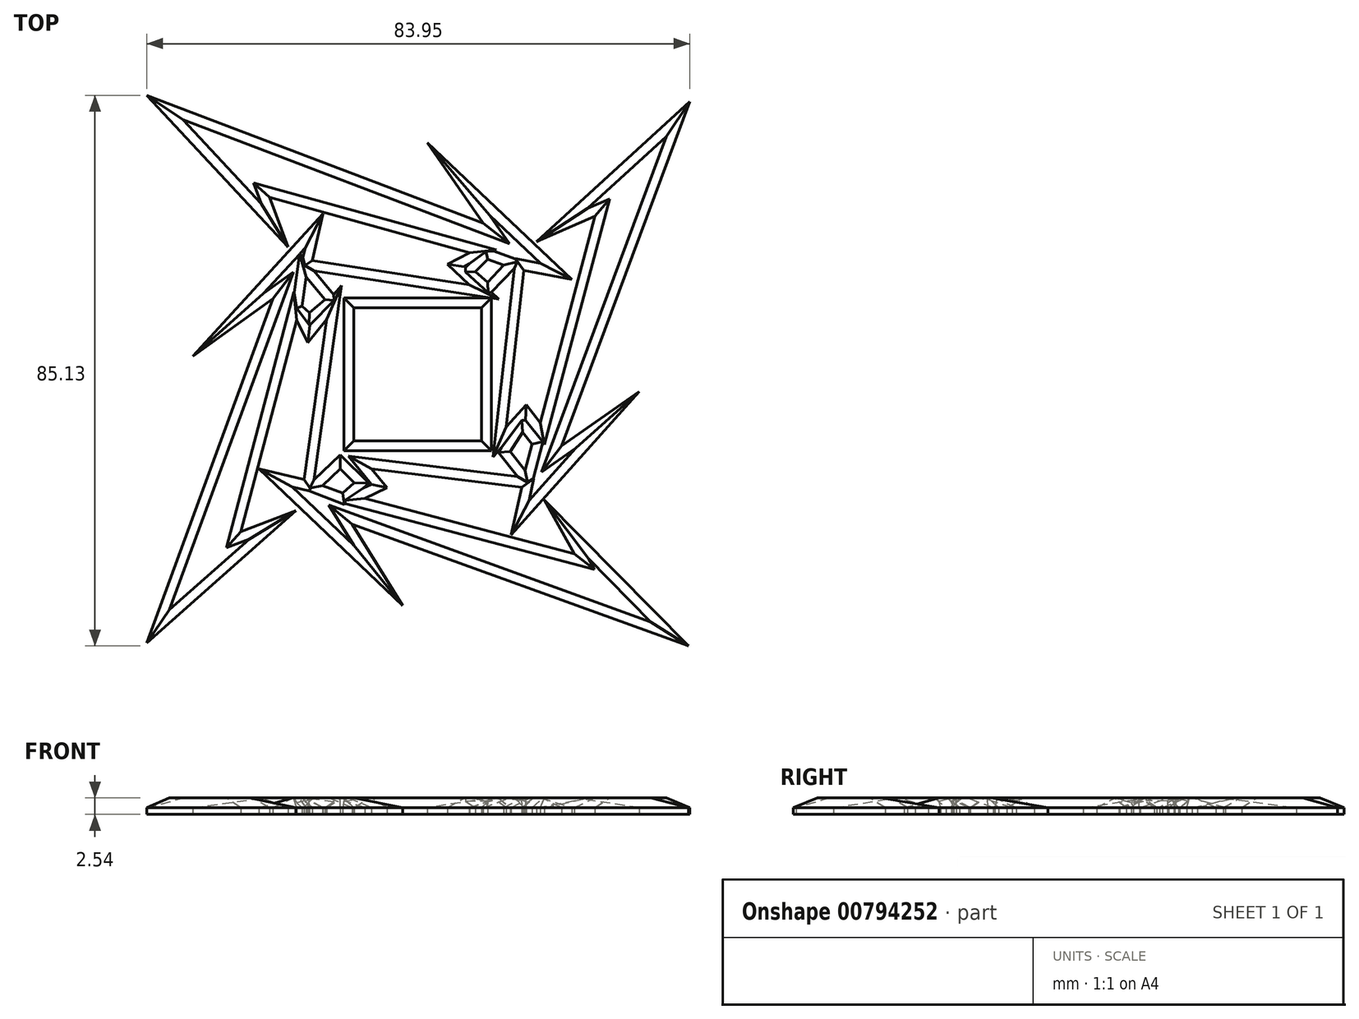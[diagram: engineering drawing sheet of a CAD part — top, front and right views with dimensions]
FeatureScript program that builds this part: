
annotation { "Feature Type Name" : "Feature", "Feature Type Description" : "" }
export const myFeature = defineFeature(function(context is Context, id is Id, definition is map)
    precondition{}
    {
        {
            var Q0;
            Q0=qCreatedBy(makeId("Top.planeOp"),FACE);
            var sketch = newSketch(context, id + "F0", { "sketchPlane" : qUnion([Q0])});
            skLineSegment(sketch, "E0", {"start": v(-34.9, 3.4) * mm, "end": v(-22.53, 12.24) * mm});
            skLineSegment(sketch, "E1", {"start": v(-22.53, 12.24) * mm, "end": v(-42.04, -40.95) * mm});
            skLineSegment(sketch, "E2", {"start": v(-42.04, -40.95) * mm, "end": v(-18.95, -20.5) * mm});
            skLineSegment(sketch, "E3", {"start": v(-18.95, -20.5) * mm, "end": v(-27.52, -23.74) * mm});
            skLineSegment(sketch, "E4", {"start": v(-18.87, 8.96) * mm, "end": v(-17.14, 5.48) * mm});
            skLineSegment(sketch, "E5", {"start": v(-17.14, 5.48) * mm, "end": v(-14.24, 9.08) * mm});
            skLineSegment(sketch, "E6", {"start": v(-14.24, 9.08) * mm, "end": v(-17.7, -15.71) * mm});
            skLineSegment(sketch, "E7", {"start": v(-17.7, -15.71) * mm, "end": v(-24.7, -14.04) * mm});
            skLineSegment(sketch, "E8", {"start": v(-24.7, -14.04) * mm, "end": v(-2.46, -35.16) * mm});
            skLineSegment(sketch, "E9", {"start": v(-2.46, -35.16) * mm, "end": v(-10.3, -22.58) * mm});
            skLineSegment(sketch, "E10", {"start": v(-10.3, -22.58) * mm, "end": v(41.73, -41.42) * mm});
            skLineSegment(sketch, "E11", {"start": v(41.73, -41.42) * mm, "end": v(19.46, -18.88) * mm});
            skLineSegment(sketch, "E12", {"start": v(19.46, -18.88) * mm, "end": v(24.08, -27.17) * mm});
            skLineSegment(sketch, "E13", {"start": v(24.08, -27.17) * mm, "end": v(-8.32, -18.6) * mm});
            skLineSegment(sketch, "E14", {"start": v(-8.32, -18.6) * mm, "end": v(-4.87, -16.98) * mm});
            skLineSegment(sketch, "E15", {"start": v(-4.87, -16.98) * mm, "end": v(-7.28, -14.04) * mm});
            skLineSegment(sketch, "E16", {"start": v(-7.28, -14.04) * mm, "end": v(15.96, -16.86) * mm});
            skLineSegment(sketch, "E17", {"start": v(15.96, -16.86) * mm, "end": v(14.3, -24.29) * mm});
            skLineSegment(sketch, "E18", {"start": v(34.13, -2.07) * mm, "end": v(22.1, -10.48) * mm});
            skLineSegment(sketch, "E19", {"start": v(22.1, -10.48) * mm, "end": v(41.9, 42.75) * mm});
            skLineSegment(sketch, "E20", {"start": v(41.9, 42.75) * mm, "end": v(18.25, 21.08) * mm});
            skLineSegment(sketch, "E21", {"start": v(18.25, 21.08) * mm, "end": v(27.23, 25.04) * mm});
            skLineSegment(sketch, "E22", {"start": v(27.23, 25.04) * mm, "end": v(18.78, -6.94) * mm});
            skLineSegment(sketch, "E23", {"start": v(18.78, -6.94) * mm, "end": v(16.6, -4.14) * mm});
            skLineSegment(sketch, "E24", {"start": v(16.6, -4.14) * mm, "end": v(13.54, -7.58) * mm});
            skLineSegment(sketch, "E25", {"start": v(13.54, -7.58) * mm, "end": v(16.28, 16.65) * mm});
            skLineSegment(sketch, "E26", {"start": v(16.28, 16.65) * mm, "end": v(23.7, 15.23) * mm});
            skLineSegment(sketch, "E27", {"start": v(1.34, 36.4) * mm, "end": v(10, 23.93) * mm});
            skLineSegment(sketch, "E28", {"start": v(10, 23.93) * mm, "end": v(-42.03, 43.71) * mm});
            skLineSegment(sketch, "E29", {"start": v(-42.03, 43.71) * mm, "end": v(-20.2, 20.25) * mm});
            skLineSegment(sketch, "E30", {"start": v(-20.2, 20.25) * mm, "end": v(-23.08, 27.92) * mm});
            skLineSegment(sketch, "E31", {"start": v(-23.08, 27.92) * mm, "end": v(7.87, 19.39) * mm});
            skLineSegment(sketch, "E32", {"start": v(7.87, 19.39) * mm, "end": v(4.46, 17.59) * mm});
            skLineSegment(sketch, "E33", {"start": v(4.46, 17.59) * mm, "end": v(7.8, 14.42) * mm});
            skLineSegment(sketch, "E34", {"start": v(7.8, 14.42) * mm, "end": v(-16.43, 18.17) * mm});
            skLineSegment(sketch, "E35", {"start": v(-16.43, 18.17) * mm, "end": v(-14.77, 25.4) * mm});
            skLineSegment(sketch, "E36", {"start": v(-17.38, 15.65) * mm, "end": v(-18.02, 11.13) * mm});
            skLineSegment(sketch, "E37", {"start": v(-18.02, 11.13) * mm, "end": v(-16.9, 10.1) * mm});
            skLineSegment(sketch, "E38", {"start": v(-16.9, 10.1) * mm, "end": v(-14.46, 12.13) * mm});
            skLineSegment(sketch, "E39", {"start": v(-14.46, 12.13) * mm, "end": v(-17.38, 15.65) * mm});
            skLineSegment(sketch, "E40", {"start": v(-12.15, -14.02) * mm, "end": v(-9.94, -16.2) * mm});
            skLineSegment(sketch, "E41", {"start": v(-9.94, -16.2) * mm, "end": v(-11.77, -17.8) * mm});
            skLineSegment(sketch, "E42", {"start": v(-11.77, -17.8) * mm, "end": v(-14.87, -16.61) * mm});
            skLineSegment(sketch, "E43", {"start": v(-14.87, -16.61) * mm, "end": v(-12.15, -14.02) * mm});
            skLineSegment(sketch, "E44", {"start": v(16.06, -8.37) * mm, "end": v(17.55, -10.21) * mm});
            skLineSegment(sketch, "E45", {"start": v(17.55, -10.21) * mm, "end": v(16.47, -14.27) * mm});
            skLineSegment(sketch, "E46", {"start": v(16.47, -14.27) * mm, "end": v(14.16, -11.37) * mm});
            skLineSegment(sketch, "E47", {"start": v(14.16, -11.37) * mm, "end": v(16.06, -8.37) * mm});
            skLineSegment(sketch, "E48", {"start": v(10.69, 18.37) * mm, "end": v(13.16, 17.46) * mm});
            skLineSegment(sketch, "E49", {"start": v(13.16, 17.46) * mm, "end": v(10.64, 14.8) * mm});
            skLineSegment(sketch, "E50", {"start": v(10.64, 14.8) * mm, "end": v(8.78, 16.45) * mm});
            skLineSegment(sketch, "E51", {"start": v(8.78, 16.45) * mm, "end": v(10.69, 18.37) * mm});
            skLineSegment(sketch, "E52", {"start": v(-10.06, 10.84) * mm, "end": v(9.71, 10.84) * mm});
            skPoint(sketch, "E52.endSnap0", {"position": v(9.71, 15.62) * mm});
            skLineSegment(sketch, "E53", {"start": v(9.71, 10.84) * mm, "end": v(9.71, -9.7) * mm});
            skLineSegment(sketch, "E54", {"start": v(9.71, -9.7) * mm, "end": v(-10, -9.7) * mm});
            skLineSegment(sketch, "E55", {"start": v(-10, -9.7) * mm, "end": v(-10.06, 10.84) * mm});
            skLineSegment(sketch, "E56", {"start": v(-27.52, -23.74) * mm, "end": v(-18.87, 8.96) * mm});
            skLineSegment(sketch, "E57", {"start": v(1.34, 36.4) * mm, "end": v(23.7, 15.23) * mm});
            skLineSegment(sketch, "E58", {"start": v(14.3, -24.29) * mm, "end": v(34.13, -2.07) * mm});
            skLineSegment(sketch, "E59", {"start": v(-14.77, 25.4) * mm, "end": v(-34.9, 3.4) * mm});
            skSolve(sketch);
        }
        {
            var Q0;
            Q0=makeQuery(id+"F0.imprint","IMPRINT",FACE,{"disambiguationData":[TD([[makeQuery(id+"F0.imprint","IMPRINT",EDGE,{"derivedFrom":sQuery(id+"F0.wireOp",EDGE,"E0")}),1.0]])]});
            extrude(context, id + "F1", {"entities" : qUnion([Q0]), "depth" : 2.54 * mm, "offsetDistance" : 25.4 * mm});
        }
        {
            var Q0;
            Q0=makeQuery(id+"F1.opExtrude","CAP_FACE",FACE,{"disambiguationData":[OSD([sQuery(id+"F0.wireOp",EDGE,"E0"),sQuery(id+"F0.wireOp",EDGE,"E1"),sQuery(id+"F0.wireOp",EDGE,"E2"),sQuery(id+"F0.wireOp",EDGE,"E3"),sQuery(id+"F0.wireOp",EDGE,"E4"),sQuery(id+"F0.wireOp",EDGE,"E5"),sQuery(id+"F0.wireOp",EDGE,"E6"),sQuery(id+"F0.wireOp",EDGE,"E7"),sQuery(id+"F0.wireOp",EDGE,"E8"),sQuery(id+"F0.wireOp",EDGE,"E9"),sQuery(id+"F0.wireOp",EDGE,"E10"),sQuery(id+"F0.wireOp",EDGE,"E11"),sQuery(id+"F0.wireOp",EDGE,"E12"),sQuery(id+"F0.wireOp",EDGE,"E13"),sQuery(id+"F0.wireOp",EDGE,"E14"),sQuery(id+"F0.wireOp",EDGE,"E15"),sQuery(id+"F0.wireOp",EDGE,"E16"),sQuery(id+"F0.wireOp",EDGE,"E17"),sQuery(id+"F0.wireOp",EDGE,"E18"),sQuery(id+"F0.wireOp",EDGE,"E19"),sQuery(id+"F0.wireOp",EDGE,"E20"),sQuery(id+"F0.wireOp",EDGE,"E21"),sQuery(id+"F0.wireOp",EDGE,"E22"),sQuery(id+"F0.wireOp",EDGE,"E23"),sQuery(id+"F0.wireOp",EDGE,"E24"),sQuery(id+"F0.wireOp",EDGE,"E25"),sQuery(id+"F0.wireOp",EDGE,"E26"),sQuery(id+"F0.wireOp",EDGE,"E27"),sQuery(id+"F0.wireOp",EDGE,"E28"),sQuery(id+"F0.wireOp",EDGE,"E29"),sQuery(id+"F0.wireOp",EDGE,"E30"),sQuery(id+"F0.wireOp",EDGE,"E31"),sQuery(id+"F0.wireOp",EDGE,"E32"),sQuery(id+"F0.wireOp",EDGE,"E33"),sQuery(id+"F0.wireOp",EDGE,"E34"),sQuery(id+"F0.wireOp",EDGE,"E35"),sQuery(id+"F0.wireOp",EDGE,"E36"),sQuery(id+"F0.wireOp",EDGE,"E37"),sQuery(id+"F0.wireOp",EDGE,"E38"),sQuery(id+"F0.wireOp",EDGE,"E39"),sQuery(id+"F0.wireOp",EDGE,"E40"),sQuery(id+"F0.wireOp",EDGE,"E41"),sQuery(id+"F0.wireOp",EDGE,"E42"),sQuery(id+"F0.wireOp",EDGE,"E43"),sQuery(id+"F0.wireOp",EDGE,"E44"),sQuery(id+"F0.wireOp",EDGE,"E45"),sQuery(id+"F0.wireOp",EDGE,"E46"),sQuery(id+"F0.wireOp",EDGE,"E47"),sQuery(id+"F0.wireOp",EDGE,"E48"),sQuery(id+"F0.wireOp",EDGE,"E49"),sQuery(id+"F0.wireOp",EDGE,"E50"),sQuery(id+"F0.wireOp",EDGE,"E51"),sQuery(id+"F0.wireOp",EDGE,"E52"),sQuery(id+"F0.wireOp",EDGE,"E53"),sQuery(id+"F0.wireOp",EDGE,"E54"),sQuery(id+"F0.wireOp",EDGE,"E55"),sQuery(id+"F0.wireOp",EDGE,"E56"),sQuery(id+"F0.wireOp",EDGE,"E57"),sQuery(id+"F0.wireOp",EDGE,"E58"),sQuery(id+"F0.wireOp",EDGE,"E59")])],"isStart":false});
            chamfer(context, id + "F2", {"entities" : qUnion([Q0]), "width" : 1.52 * mm, "tangentPropagation" : true});
        }
    });
